# Revit family: BORGE_Ограждение кровельное
name_source: partatom
category: Обобщенные модели
units: mm (PartAtom-declared; Revit-internal decimal feet)

## family parameters
Всегда вертикально = Нет
Заголовок OmniClass = Diffusers, Registers, and Grilles
Может служить основой для арматурных стержней = Нет
На основе рабочей плоскости = Да
Номер OmniClass = 23.75.70.21.27.11
Общий = Нет
При загрузке вырезать с полостями = Нет
Размер круглого соединителя = Использовать диаметр
Тип детали = Нормальный
Точка расчета площади = Да

## types (66) — shared parameters
ADSK_URL документации изделия = https://borge.ru
ADSK_URL страницы изделия = https://borge.pro
ADSK_Версия семейства = Rev1 2023-08
BIM Support_Разрабочик = BIM Support
BIM Support_Сайт = https://www.bim-support.ru
BORGE_Единица измерения_м = Нет
BORGE_Единица измерения_шт = Да
LT = BORGE_Ограждение
URL = https://borge.ru
Изготовитель = ООО «Борге», ООО «Бипро»
zero-valued in all types: Отметка по умолчанию

## per-type parameters (varying)
| type | ADSK_Масса_Текст | ADSK_Материал | Code1 | Code2 | H | h1 |
| Ограждение кровельное_H-60_Бело-алюминиевый_RAL 9006 | 13 | BOGRE_Уловный_Антрацитово-серый_RAL 7016 | 1 | 1 | 634 мм | 918 мм |
| Ограждение кровельное_H-60_Чёрный матовый_RAL 9005 | 13 | BOGRE_Уловный_Чёрный матовый_RAL 9005 | 1 | 2 | 634 мм | 250 мм |
| Ограждение кровельное_H-60_Чёрный_RAL 9005 | 13 | BOGRE_Уловный_Чёрный_RAL 9005 | 1 | 3 | 634 мм | 250 мм |
| Ограждение кровельное_H-60_Сигнально-белый_RAL 9003 | 13 | BOGRE_Уловный_Сигнально-белый_RAL 9003 | 1 | 4 | 634 мм | 250 мм |
| Ограждение кровельное_H-60_Окрашенный_NL 807 | 13 | BOGRE_Уловный_Окрашенный_NL 807 | 1 | 5 | 634 мм | 250 мм |
| Ограждение кровельное_H-60_Окрашенный_NL 805 | 13 | BOGRE_Уловный_Окрашенный_NL 805 | 1 | 6 | 634 мм | 250 мм |
| Ограждение кровельное_H-60_Серо-коричневый матовый_RAL 8019 | 13 | BOGRE_Уловный_Серо-коричневый матовый_RAL 8019 | 1 | 7 | 634 мм | 250 мм |
| Ограждение кровельное_H-60_Серо-коричневый_RAL 8019 | 13 | BOGRE_Уловный_Серо-коричневый_RAL 8019 | 1 | 8 | 634 мм | 250 мм |
| Ограждение кровельное_H-60_Коричневый шоколад матовый_RAL 8017 | 13 | BOGRE_Уловный_Коричневый шоколад матовый_RAL 8017 | 1 | 9 | 634 мм | 250 мм |
| Ограждение кровельное_H-60_Коричневый шоколад_RAL 8017 | 13 | BOGRE_Уловный_Коричневый шоколад_RAL 8017 | 1 | 10 | 634 мм | 250 мм |
| Ограждение кровельное_H-60_Терракотовый_RAL 8004 | 13 | BOGRE_Уловный_Терракотовый_RAL 8004 | 1 | 11 | 634 мм | 250 мм |
| Ограждение кровельное_H-60_Серый графит матовый_RAL 7024 | 13 | BOGRE_Уловный_Серый графит матовый_RAL 7024 | 1 | 12 | 634 мм | 250 мм |
| Ограждение кровельное_H-60_Серый графит_RAL 7024 | 13 | BOGRE_Уловный_Серый графит_RAL 7024 | 1 | 13 | 634 мм | 250 мм |
| Ограждение кровельное_H-60_Антрацитово-серый_RAL 7016 | 13 | BOGRE_Уловный_Антрацитово-серый_RAL 7016 | 1 | 14 | 634 мм | 250 мм |
| Ограждение кровельное_H-60_Сигнально-серый_RAL 7004 | 13 | BOGRE_Уловный_Сигнально-серый_RAL 7004 | 1 | 15 | 634 мм | 250 мм |
| Ограждение кровельное_H-60_Зелёный мох_RAL 6005 | 13 | BOGRE_Уловный_Зелёный мох_RAL 6005 | 1 | 16 | 634 мм | 250 мм |
| Ограждение кровельное_H-60_Лиственно-зеленый_RAL 6002 | 13 | BOGRE_Уловный_Лиственно-зеленый_RAL 6002 | 1 | 17 | 634 мм | 250 мм |
| Ограждение кровельное_H-60_Сигнально-синий_RAL 5005 | 13 | BOGRE_Уловный_Сигнально-синий_RAL 5005 | 1 | 18 | 634 мм | 250 мм |
| Ограждение кровельное_H-60_Серо-коричневый_RR 32 | 13 | BOGRE_Уловный_Серо-коричневый_RR 32 | 1 | 19 | 634 мм | 250 мм |
| Ограждение кровельное_H-60_Коричнево-красный_RAL 3011 | 13 | BOGRE_Уловный_Коричнево-красный_RAL 3011 | 1 | 20 | 634 мм | 250 мм |
| Ограждение кровельное_H-60_Красное вино_RAL 3005 | 13 | BOGRE_Уловный_Красное вино_RAL 3005 | 1 | 21 | 634 мм | 250 мм |
| Ограждение кровельное_H-60_Рубиново-красный_RAL 3003 | 13 | BOGRE_Уловный_Рубиново-красный_RAL 3003 | 1 | 22 | 634 мм | 250 мм |
| Ограждение кровельное_H-90_Бело-алюминиевый_RAL 9006 | 14 | BOGRE_Уловный_Бело-алюминиевый_RAL 9006 | 2 | 23 | 934 мм | 350 мм |
| Ограждение кровельное_H-90_Чёрный матовый_RAL 9005 | 14 | BOGRE_Уловный_Чёрный матовый_RAL 9005 | 2 | 24 | 934 мм | 350 мм |
| Ограждение кровельное_H-90_Чёрный_RAL 9005 | 14 | BOGRE_Уловный_Чёрный_RAL 9005 | 2 | 25 | 934 мм | 350 мм |
| Ограждение кровельное_H-90_Сигнально-белый_RAL 9003 | 14 | BOGRE_Уловный_Сигнально-белый_RAL 9003 | 2 | 26 | 934 мм | 350 мм |
| Ограждение кровельное_H-90_Окрашенный_NL 807 | 14 | BOGRE_Уловный_Окрашенный_NL 807 | 2 | 27 | 934 мм | 350 мм |
| Ограждение кровельное_H-90_Окрашенный_NL 805 | 14 | BOGRE_Уловный_Окрашенный_NL 805 | 2 | 28 | 934 мм | 350 мм |
| Ограждение кровельное_H-90_Серо-коричневый матовый_RAL 8019 | 14 | BOGRE_Уловный_Серо-коричневый матовый_RAL 8019 | 2 | 29 | 934 мм | 350 мм |
| Ограждение кровельное_H-90_Серо-коричневый_RAL 8019 | 14 | BOGRE_Уловный_Серо-коричневый_RAL 8019 | 2 | 30 | 934 мм | 350 мм |
| Ограждение кровельное_H-90_Коричневый шоколад матовый_RAL 8017 | 14 | BOGRE_Уловный_Коричневый шоколад матовый_RAL 8017 | 2 | 31 | 934 мм | 350 мм |
| Ограждение кровельное_H-90_Коричневый шоколад_RAL 8017 | 14 | BOGRE_Уловный_Коричневый шоколад_RAL 8017 | 2 | 32 | 934 мм | 350 мм |
| Ограждение кровельное_H-90_Терракотовый_RAL 8004 | 14 | BOGRE_Уловный_Терракотовый_RAL 8004 | 2 | 33 | 934 мм | 350 мм |
| Ограждение кровельное_H-90_Серый графит матовый_RAL 7024 | 14 | BOGRE_Уловный_Серый графит матовый_RAL 7024 | 2 | 34 | 934 мм | 350 мм |
| Ограждение кровельное_H-90_Серый графит_RAL 7024 | 14 | BOGRE_Уловный_Серый графит_RAL 7024 | 2 | 35 | 934 мм | 350 мм |
| Ограждение кровельное_H-90_Антрацитово-серый_RAL 7016 | 14 | BOGRE_Уловный_Антрацитово-серый_RAL 7016 | 2 | 36 | 934 мм | 200 мм |
| Ограждение кровельное_H-90_Сигнально-серый_RAL 7004 | 14 | BOGRE_Уловный_Сигнально-серый_RAL 7004 | 2 | 37 | 934 мм | 350 мм |
| Ограждение кровельное_H-90_Зелёный мох_RAL 6005 | 14 | BOGRE_Уловный_Зелёный мох_RAL 6005 | 2 | 38 | 934 мм | 350 мм |
| Ограждение кровельное_H-90_Лиственно-зеленый_RAL 6002 | 14 | BOGRE_Уловный_Лиственно-зеленый_RAL 6002 | 2 | 39 | 934 мм | 350 мм |
| Ограждение кровельное_H-90_Сигнально-синий_RAL 5005 | 14 | BOGRE_Уловный_Сигнально-синий_RAL 5005 | 2 | 40 | 934 мм | 350 мм |
| Ограждение кровельное_H-90_Серо-коричневый_RR 32 | 14 | BOGRE_Уловный_Серо-коричневый_RR 32 | 2 | 41 | 934 мм | 350 мм |
| Ограждение кровельное_H-90_Коричнево-красный_RAL 3011 | 14 | BOGRE_Уловный_Коричнево-красный_RAL 3011 | 2 | 42 | 934 мм | 350 мм |
| Ограждение кровельное_H-90_Красное вино_RAL 3005 | 14 | BOGRE_Уловный_Красное вино_RAL 3005 | 2 | 43 | 934 мм | 350 мм |
| Ограждение кровельное_H-90_Рубиново-красный_RAL 3003 | 14 | BOGRE_Уловный_Рубиново-красный_RAL 3003 | 2 | 44 | 934 мм | 350 мм |
| Ограждение кровельное_H-120_Бело-алюминиевый_RAL 9006 | 16 | BOGRE_Уловный_Бело-алюминиевый_RAL 9006 | 3 | 45 | 1234 мм | 350 мм |
| Ограждение кровельное_H-120_Чёрный матовый_RAL 9005 | 16 | BOGRE_Уловный_Чёрный матовый_RAL 9005 | 3 | 46 | 1234 мм | 300 мм |
| Ограждение кровельное_H-120_Чёрный_RAL 9005 | 16 | BOGRE_Уловный_Чёрный_RAL 9005 | 3 | 47 | 1234 мм | 350 мм |
| Ограждение кровельное_H-120_Сигнально-белый_RAL 9003 | 16 | BOGRE_Уловный_Сигнально-белый_RAL 9003 | 3 | 48 | 1234 мм | 350 мм |
| Ограждение кровельное_H-120_Окрашенный_NL 807 | 16 | BOGRE_Уловный_Окрашенный_NL 807 | 3 | 49 | 1234 мм | 350 мм |
| Ограждение кровельное_H-120_Окрашенный_NL 805 | 16 | BOGRE_Уловный_Окрашенный_NL 805 | 3 | 50 | 1234 мм | 350 мм |
| Ограждение кровельное_H-120_Серо-коричневый матовый_RAL 8019 | 16 | BOGRE_Уловный_Серо-коричневый матовый_RAL 8019 | 3 | 51 | 1234 мм | 350 мм |
| Ограждение кровельное_H-120_Серо-коричневый_RAL 8019 | 16 | BOGRE_Уловный_Серо-коричневый_RAL 8019 | 3 | 52 | 1234 мм | 350 мм |
| Ограждение кровельное_H-120_Коричневый шоколад матовый_RAL 8017 | 16 | BOGRE_Уловный_Коричневый шоколад матовый_RAL 8017 | 3 | 53 | 1234 мм | 350 мм |
| Ограждение кровельное_H-120_Коричневый шоколад_RAL 8017 | 16 | BOGRE_Уловный_Коричневый шоколад_RAL 8017 | 3 | 54 | 1234 мм | 350 мм |
| Ограждение кровельное_H-120_Терракотовый_RAL 8004 | 16 | BOGRE_Уловный_Терракотовый_RAL 8004 | 3 | 55 | 1234 мм | 350 мм |
| Ограждение кровельное_H-120_Серый графит матовый_RAL 7024 | 16 | BOGRE_Уловный_Серый графит матовый_RAL 7024 | 3 | 56 | 1234 мм | 350 мм |
| Ограждение кровельное_H-120_Серый графит_RAL 7024 | 16 | BOGRE_Уловный_Серый графит_RAL 7024 | 3 | 57 | 1234 мм | 350 мм |
| Ограждение кровельное_H-120_Антрацитово-серый_RAL 7016 | 16 | BOGRE_Уловный_Антрацитово-серый_RAL 7016 | 3 | 58 | 1234 мм | 350 мм |
| Ограждение кровельное_H-120_Сигнально-серый_RAL 7004 | 16 | BOGRE_Уловный_Сигнально-серый_RAL 7004 | 3 | 59 | 1234 мм | 350 мм |
| Ограждение кровельное_H-120_Зелёный мох_RAL 6005 | 16 | BOGRE_Уловный_Зелёный мох_RAL 6005 | 3 | 60 | 1234 мм | 350 мм |
| Ограждение кровельное_H-120_Лиственно-зеленый_RAL 6002 | 16 | BOGRE_Уловный_Лиственно-зеленый_RAL 6002 | 3 | 61 | 1234 мм | 350 мм |
| Ограждение кровельное_H-120_Сигнально-синий_RAL 5005 | 16 | BOGRE_Уловный_Сигнально-синий_RAL 5005 | 3 | 62 | 1234 мм | 350 мм |
| Ограждение кровельное_H-120_Серо-коричневый_RR 32 | 16 | BOGRE_Уловный_Серо-коричневый_RR 32 | 3 | 63 | 1234 мм | 350 мм |
| Ограждение кровельное_H-120_Коричнево-красный_RAL 3011 | 16 | BOGRE_Уловный_Коричнево-красный_RAL 3011 | 3 | 64 | 1234 мм | 350 мм |
| Ограждение кровельное_H-120_Красное вино_RAL 3005 | 16 | BOGRE_Уловный_Красное вино_RAL 3005 | 3 | 65 | 1234 мм | 350 мм |
| Ограждение кровельное_H-120_Рубиново-красный_RAL 3003 | 16 | BOGRE_Уловный_Рубиново-красный_RAL 3003 | 3 | 66 | 1234 мм | 350 мм |
